# Revit family: Metal_Lockers-Salsbury_Industries-18_51000_Series-3_Wide_Units
name_source: partatom
category: Specialty Equipment
revit_build: Autodesk Revit 2016 (Build: 20150714_1515(x64)
units: mm (PartAtom-declared; Revit-internal decimal feet)

## family parameters
Always vertical = Yes
Cut with Voids When Loaded = No
OmniClass Number = 23.40.00.00
OmniClass Title = Equipment and Furnishings
Part Type = Normal
Room Calculation Point = No
Round Connector Dimension = Use Diameter
Shared = No
Work Plane-Based = No

## types (6) — shared parameters
Assembly Code = C1030310
Door Location D1 = Metal Locker Doors-18 inch with Hasps : Single Tier Door - 6 foot
Hasp Handle Material = Plastic - Salsbury Finish - Black
Hasp Plate Rivet Material = Steel -Salsbury Finish - Polished Steel
Manufacturer = Salsbury Industries
MasterFormat Number = 10 51 13
MasterFormat Title = Lockers
OmniClass 23 Number = 23.40.00.00
Type Comments = 18" Wide Standard Metal Lockers - Single Tier
URL = www.lockers.com
Unit Height = 72 "
Version = 2.0 (02/28/18)
Width = 54.04 "

## per-type parameters (varying)
| type | Base Height | Depth | Description | Model | OmniClass 23 Title | Sloping Corner Filler Offset | Sloping Hood Height | Standard Leg Base | Zee Base |
| 18-51361 - with Standard 6" High Legs | 6 " | 21.01 " | 3 Wide - 6 Feet High - 21 Inches Deep | 18-51361 | Equipment and Furnishings | 77.68 " | 12.796 " | Metal Locker Legs - 3 Wide : 6" High - 54"W x 21"D | Metal Locker Zee Base - 3 Wide : None |
| 18-51368 - with Standard 6" High Legs | 6 " | 18.01 " | 3 Wide - 6 Feet High - 18 Inches Deep | 18-51368 | Equipment and Furnishings | 77.68 " | 10.739 " | Metal Locker Legs - 3 Wide : 6" High - 54"W x 18"D | Metal Locker Zee Base - 3 Wide : None |
| 18-51361 - with 77575 Zee Base and 77550 Lockers without Legs | 4 " | 21.01 " | 3 Wide - 6 Feet High - 21 Inches Deep with Zee Base and Lockers without Legs | 18-51361 with 77575 and 77550 | Equipment and Furnishings | 75.68 " | 12.796 " | Metal Locker Legs - 3 Wide : No Legs | Metal Locker Zee Base - 3 Wide : 77571 - 54"W x 21"D |
| 18-51368 - with 77578 Zee Base and 77550 Lockers without Legs | 4 " | 18.01 " | 3 Wide - 6 Feet High - 18 Inches Deep with Zee Base and Lockers without Legs | 18-51368 with 77578 and 77550 | Equipment aqnd Furnishings | 75.68 " | 10.739 " | Metal Locker Legs - 3 Wide : No Legs | Metal Locker Zee Base - 3 Wide : 77578 - 54"W x 18"D |
| 18-51361 - with 77550 Lockers without Legs | 0 " | 21.01 " | 3 Wide - 6 Feet High - 21 Inches Deep with Lockers without Legs | 18-51361 with 77550 | Equipment and Furnishings | 71.68 " | 12.796 " | Metal Locker Legs - 3 Wide : No Legs | Metal Locker Zee Base - 3 Wide : None |
| 18-51368 - with 77550 Lockers without Legs | 0 " | 18.01 " | 3 Wide - 6 Feet High - 18 Inches Deep with Lockers without Legs | 18-51368 with 77550 | Equipment and Furnishings | 71.68 " | 10.739 " | Metal Locker Legs - 3 Wide : No Legs | Metal Locker Zee Base - 3 Wide : None |

## geometry (parser evidence)
native form markers: Sweep x48
no freeform markers — native parametric forms only
